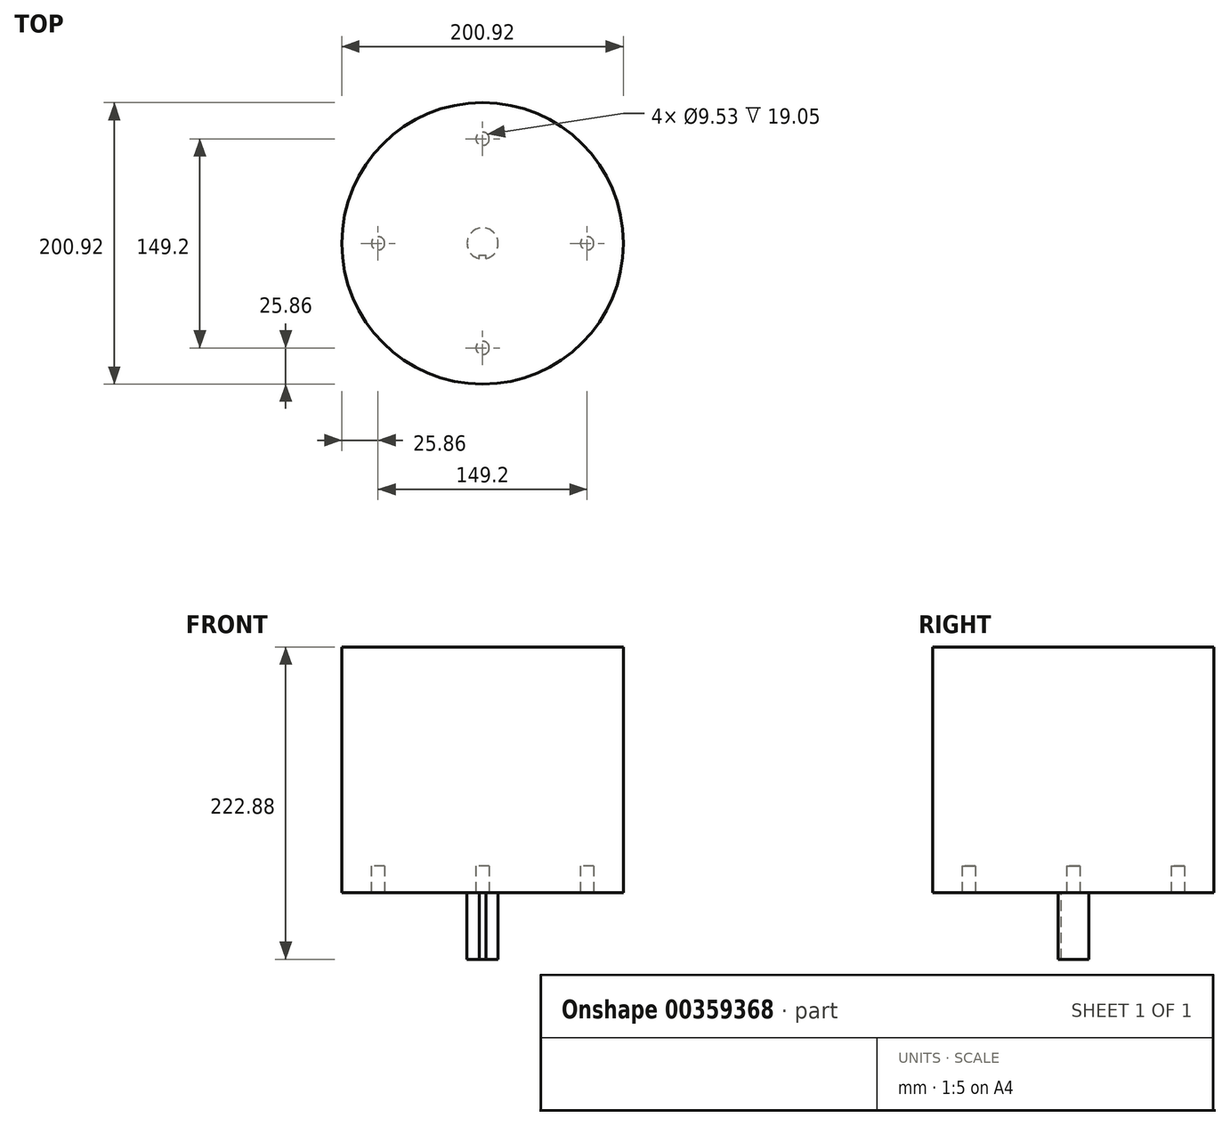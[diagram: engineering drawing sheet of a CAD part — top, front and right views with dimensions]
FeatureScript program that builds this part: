
annotation { "Feature Type Name" : "Feature", "Feature Type Description" : "" }
export const myFeature = defineFeature(function(context is Context, id is Id, definition is map)
    precondition{}
    {
        {
            var Q0;
            Q0=qCreatedBy(makeId("Top.planeOp"),FACE);
            var sketch = newSketch(context, id + "F0", { "sketchPlane" : qUnion([Q0])});
            skCircle(sketch, "E0", {"center": v(0, 0) * mm, "radius": 100.46 * mm});
            skCircle(sketch, "E1", {"center": v(0, 0) * mm, "radius": 74.6 * mm});
            skCircle(sketch, "E2", {"center": v(0, 74.6) * mm, "radius": 4.76 * mm});
            skCircle(sketch, "E3", {"center": v(74.6, 0) * mm, "radius": 4.76 * mm});
            skCircle(sketch, "E4", {"center": v(0, -74.6) * mm, "radius": 4.76 * mm});
            skCircle(sketch, "E5", {"center": v(-74.6, 0) * mm, "radius": 4.76 * mm});
            skSolve(sketch);
        }
        {
            var Q0;
            Q0=makeQuery(id+"F0.imprint","IMPRINT",FACE,{"disambiguationData":[TD([[makeQuery(id+"F0.imprint","IMPRINT",EDGE,{"derivedFrom":sQuery(id+"F0.wireOp",EDGE,"E0")}),1.0]])]});
            var Q1;
            {var subQ0=sQuery(id+"F0.wireOp",EDGE,"E5");var subQ1=sQuery(id+"F0.wireOp",EDGE,"E1");var subQ2=makeQuery(id+"F0.imprint","INTERSECT",VERTEX,{"disambiguationData":[OD(0.0)],"derivedFrom":[subQ1,subQ0]});Q1=makeQuery(id+"F0.imprint","IMPRINT",FACE,{"disambiguationData":[TD([[makeQuery(id+"F0.imprint","IMPRINT",EDGE,{"disambiguationData":[TD([[subQ2,-1.0]])],"derivedFrom":subQ1}),-1.0]])]});}
            var Q2;
            {var subQ0=sQuery(id+"F0.wireOp",EDGE,"E5");var subQ1=sQuery(id+"F0.wireOp",EDGE,"E1");var subQ2=makeQuery(id+"F0.imprint","INTERSECT",VERTEX,{"disambiguationData":[OD(0.0)],"derivedFrom":[subQ1,subQ0]});Q2=makeQuery(id+"F0.imprint","IMPRINT",FACE,{"disambiguationData":[TD([[makeQuery(id+"F0.imprint","IMPRINT",EDGE,{"disambiguationData":[TD([[subQ2,-1.0]])],"derivedFrom":subQ1}),1.0]])]});}
            var Q3;
            {var subQ0=sQuery(id+"F0.wireOp",EDGE,"E2");var subQ1=sQuery(id+"F0.wireOp",EDGE,"E1");var subQ2=makeQuery(id+"F0.imprint","INTERSECT",VERTEX,{"disambiguationData":[OD(0.0)],"derivedFrom":[subQ1,subQ0]});Q3=makeQuery(id+"F0.imprint","IMPRINT",FACE,{"disambiguationData":[TD([[makeQuery(id+"F0.imprint","IMPRINT",EDGE,{"disambiguationData":[TD([[subQ2,-1.0]])],"derivedFrom":subQ1}),-1.0]])]});}
            var Q4;
            {var subQ0=sQuery(id+"F0.wireOp",EDGE,"E2");var subQ1=sQuery(id+"F0.wireOp",EDGE,"E1");var subQ2=makeQuery(id+"F0.imprint","INTERSECT",VERTEX,{"disambiguationData":[OD(0.0)],"derivedFrom":[subQ1,subQ0]});Q4=makeQuery(id+"F0.imprint","IMPRINT",FACE,{"disambiguationData":[TD([[makeQuery(id+"F0.imprint","IMPRINT",EDGE,{"disambiguationData":[TD([[subQ2,-1.0]])],"derivedFrom":subQ1}),1.0]])]});}
            var Q5;
            {var subQ0=sQuery(id+"F0.wireOp",EDGE,"E3");var subQ1=sQuery(id+"F0.wireOp",EDGE,"E1");var subQ2=makeQuery(id+"F0.imprint","INTERSECT",VERTEX,{"disambiguationData":[OD(0.0)],"derivedFrom":[subQ1,subQ0]});Q5=makeQuery(id+"F0.imprint","IMPRINT",FACE,{"disambiguationData":[TD([[makeQuery(id+"F0.imprint","IMPRINT",EDGE,{"disambiguationData":[TD([[subQ2,1.0]])],"derivedFrom":subQ1}),1.0]])]});}
            var Q6;
            {var subQ0=sQuery(id+"F0.wireOp",EDGE,"E3");var subQ1=sQuery(id+"F0.wireOp",EDGE,"E1");var subQ2=makeQuery(id+"F0.imprint","INTERSECT",VERTEX,{"disambiguationData":[OD(0.0)],"derivedFrom":[subQ1,subQ0]});Q6=makeQuery(id+"F0.imprint","IMPRINT",FACE,{"disambiguationData":[TD([[makeQuery(id+"F0.imprint","IMPRINT",EDGE,{"disambiguationData":[TD([[subQ2,1.0]])],"derivedFrom":subQ1}),-1.0]])]});}
            var Q7;
            {var subQ0=sQuery(id+"F0.wireOp",EDGE,"E4");var subQ1=sQuery(id+"F0.wireOp",EDGE,"E1");var subQ2=makeQuery(id+"F0.imprint","INTERSECT",VERTEX,{"disambiguationData":[OD(0.0)],"derivedFrom":[subQ1,subQ0]});Q7=makeQuery(id+"F0.imprint","IMPRINT",FACE,{"disambiguationData":[TD([[makeQuery(id+"F0.imprint","IMPRINT",EDGE,{"disambiguationData":[TD([[subQ2,-1.0]])],"derivedFrom":subQ1}),-1.0]])]});}
            var Q8;
            {var subQ1=sQuery(id+"F0.wireOp",EDGE,"E1");var subQ9=sQuery(id+"F0.wireOp",EDGE,"E2");var subQ11=makeQuery(id+"F0.imprint","INTERSECT",VERTEX,{"disambiguationData":[OD(0.0)],"derivedFrom":[subQ1,subQ9]});Q8=makeQuery(id+"F0.imprint","IMPRINT",FACE,{"disambiguationData":[TD([[makeQuery(id+"F0.imprint","IMPRINT",EDGE,{"disambiguationData":[TD([[subQ11,1.0]])],"derivedFrom":subQ1}),1.0]])]});}
            var Q9;
            {var subQ0=sQuery(id+"F0.wireOp",EDGE,"E4");var subQ1=sQuery(id+"F0.wireOp",EDGE,"E1");var subQ2=makeQuery(id+"F0.imprint","INTERSECT",VERTEX,{"disambiguationData":[OD(0.0)],"derivedFrom":[subQ1,subQ0]});Q9=makeQuery(id+"F0.imprint","IMPRINT",FACE,{"disambiguationData":[TD([[makeQuery(id+"F0.imprint","IMPRINT",EDGE,{"disambiguationData":[TD([[subQ2,-1.0]])],"derivedFrom":subQ1}),1.0]])]});}
            extrude(context, id + "F1", {"entities" : qUnion([Q0, Q1, Q2, Q3, Q4, Q5, Q6, Q7, Q8, Q9]), "depth" : 175.26 * mm, "offsetDistance" : 25.4 * mm});
        }
        {
            var Q0;
            {var subQ0=sQuery(id+"F0.wireOp",EDGE,"E5");var subQ1=sQuery(id+"F0.wireOp",EDGE,"E1");var subQ2=makeQuery(id+"F0.imprint","INTERSECT",VERTEX,{"disambiguationData":[OD(0.0)],"derivedFrom":[subQ1,subQ0]});Q0=makeQuery(id+"F0.imprint","IMPRINT",FACE,{"disambiguationData":[TD([[makeQuery(id+"F0.imprint","IMPRINT",EDGE,{"disambiguationData":[TD([[subQ2,-1.0]])],"derivedFrom":subQ1}),1.0]])]});}
            var Q1;
            {var subQ0=sQuery(id+"F0.wireOp",EDGE,"E5");var subQ1=sQuery(id+"F0.wireOp",EDGE,"E1");var subQ2=makeQuery(id+"F0.imprint","INTERSECT",VERTEX,{"disambiguationData":[OD(0.0)],"derivedFrom":[subQ1,subQ0]});Q1=makeQuery(id+"F0.imprint","IMPRINT",FACE,{"disambiguationData":[TD([[makeQuery(id+"F0.imprint","IMPRINT",EDGE,{"disambiguationData":[TD([[subQ2,-1.0]])],"derivedFrom":subQ1}),-1.0]])]});}
            var Q2;
            {var subQ0=sQuery(id+"F0.wireOp",EDGE,"E2");var subQ1=sQuery(id+"F0.wireOp",EDGE,"E1");var subQ2=makeQuery(id+"F0.imprint","INTERSECT",VERTEX,{"disambiguationData":[OD(0.0)],"derivedFrom":[subQ1,subQ0]});Q2=makeQuery(id+"F0.imprint","IMPRINT",FACE,{"disambiguationData":[TD([[makeQuery(id+"F0.imprint","IMPRINT",EDGE,{"disambiguationData":[TD([[subQ2,-1.0]])],"derivedFrom":subQ1}),1.0]])]});}
            var Q3;
            {var subQ0=sQuery(id+"F0.wireOp",EDGE,"E2");var subQ1=sQuery(id+"F0.wireOp",EDGE,"E1");var subQ2=makeQuery(id+"F0.imprint","INTERSECT",VERTEX,{"disambiguationData":[OD(0.0)],"derivedFrom":[subQ1,subQ0]});Q3=makeQuery(id+"F0.imprint","IMPRINT",FACE,{"disambiguationData":[TD([[makeQuery(id+"F0.imprint","IMPRINT",EDGE,{"disambiguationData":[TD([[subQ2,-1.0]])],"derivedFrom":subQ1}),-1.0]])]});}
            var Q4;
            {var subQ0=sQuery(id+"F0.wireOp",EDGE,"E3");var subQ1=sQuery(id+"F0.wireOp",EDGE,"E1");var subQ2=makeQuery(id+"F0.imprint","INTERSECT",VERTEX,{"disambiguationData":[OD(0.0)],"derivedFrom":[subQ1,subQ0]});Q4=makeQuery(id+"F0.imprint","IMPRINT",FACE,{"disambiguationData":[TD([[makeQuery(id+"F0.imprint","IMPRINT",EDGE,{"disambiguationData":[TD([[subQ2,1.0]])],"derivedFrom":subQ1}),1.0]])]});}
            var Q5;
            {var subQ0=sQuery(id+"F0.wireOp",EDGE,"E3");var subQ1=sQuery(id+"F0.wireOp",EDGE,"E1");var subQ2=makeQuery(id+"F0.imprint","INTERSECT",VERTEX,{"disambiguationData":[OD(0.0)],"derivedFrom":[subQ1,subQ0]});Q5=makeQuery(id+"F0.imprint","IMPRINT",FACE,{"disambiguationData":[TD([[makeQuery(id+"F0.imprint","IMPRINT",EDGE,{"disambiguationData":[TD([[subQ2,1.0]])],"derivedFrom":subQ1}),-1.0]])]});}
            var Q6;
            {var subQ0=sQuery(id+"F0.wireOp",EDGE,"E4");var subQ1=sQuery(id+"F0.wireOp",EDGE,"E1");var subQ2=makeQuery(id+"F0.imprint","INTERSECT",VERTEX,{"disambiguationData":[OD(0.0)],"derivedFrom":[subQ1,subQ0]});Q6=makeQuery(id+"F0.imprint","IMPRINT",FACE,{"disambiguationData":[TD([[makeQuery(id+"F0.imprint","IMPRINT",EDGE,{"disambiguationData":[TD([[subQ2,-1.0]])],"derivedFrom":subQ1}),-1.0]])]});}
            var Q7;
            {var subQ0=sQuery(id+"F0.wireOp",EDGE,"E4");var subQ1=sQuery(id+"F0.wireOp",EDGE,"E1");var subQ2=makeQuery(id+"F0.imprint","INTERSECT",VERTEX,{"disambiguationData":[OD(0.0)],"derivedFrom":[subQ1,subQ0]});Q7=makeQuery(id+"F0.imprint","IMPRINT",FACE,{"disambiguationData":[TD([[makeQuery(id+"F0.imprint","IMPRINT",EDGE,{"disambiguationData":[TD([[subQ2,-1.0]])],"derivedFrom":subQ1}),1.0]])]});}
            extrude(context, id + "F2", {"entities" : qUnion([Q0, Q1, Q2, Q3, Q4, Q5, Q6, Q7]), "operationType" : NewBodyOperationType.REMOVE, "depth" : 19.05 * mm, "offsetDistance" : 25.4 * mm});
        }
        {
            var Q0;
            {var subQ1=sQuery(id+"F0.wireOp",EDGE,"E1");var subQ9=sQuery(id+"F0.wireOp",EDGE,"E2");var subQ11=makeQuery(id+"F0.imprint","INTERSECT",VERTEX,{"disambiguationData":[OD(0.0)],"derivedFrom":[subQ1,subQ9]});Q0=makeQuery(id+"F0.imprint","IMPRINT",FACE,{"disambiguationData":[TD([[makeQuery(id+"F0.imprint","IMPRINT",EDGE,{"disambiguationData":[TD([[subQ11,1.0]])],"derivedFrom":subQ1}),1.0]])]});}
            var sketch = newSketch(context, id + "F3", { "sketchPlane" : qUnion([Q0])});
            skCircle(sketch, "E6", {"center": v(0, 0) * mm, "radius": 11.11 * mm});
            skLineSegment(sketch, "E7.bottom", {"start": v(-2.39, -11.11) * mm, "end": v(2.39, -11.11) * mm});
            skLineSegment(sketch, "E7.top", {"start": v(-2.39, -8.46) * mm, "end": v(2.39, -8.46) * mm});
            skLineSegment(sketch, "E7.left", {"start": v(-2.39, -11.11) * mm, "end": v(-2.39, -8.46) * mm});
            skLineSegment(sketch, "E7.right", {"start": v(2.39, -11.11) * mm, "end": v(2.39, -8.46) * mm});
            skSolve(sketch);
        }
        {
            var Q0;
            {var subQ5=sQuery(id+"F3.wireOp",EDGE,"E7.top");Q0=makeQuery(id+"F3.imprint","IMPRINT",FACE,{"disambiguationData":[TD([[makeQuery(id+"F3.imprint","IMPRINT",EDGE,{"derivedFrom":subQ5}),1.0]])]});}
            var Q1;
            Q1=sQuery(id+"F3.wireOp",EDGE,"E6");
            extrude(context, id + "F4", {"entities" : qUnion([Q0]), "operationType" : NewBodyOperationType.ADD, "surfaceEntities" : qUnion([Q1]), "oppositeDirection" : true, "depth" : 47.62 * mm, "offsetDistance" : 25.4 * mm});
        }
    });
